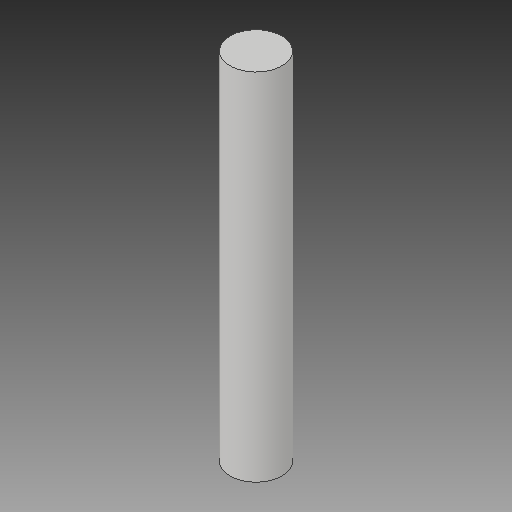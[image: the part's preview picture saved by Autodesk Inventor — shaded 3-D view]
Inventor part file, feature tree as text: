
AUTODESK INVENTOR PART (.ipt)
format: ipt  version: 2017 (Build 210142000, 142)  size: 85,504 bytes
history: native  units: in
note: dims shown in document units (in); Inventor stores cm internally (conversion verified against a paired STEP export)
features: extrude x1, sketch x1
ambient origin geometry x8: Origin, YZ Plane, XZ Plane, XY Plane, X Axis, Y Axis, Z Axis, Center Point
bodies: Solid1 (feature_tree)
feature tree (2):
  extrude  "Extrusion1"  Depth=1.0in TaperAngle=0.0deg
  sketch  "Sketch1"  dims[d0=0.146in d1=1.0in d2=0.0in]
